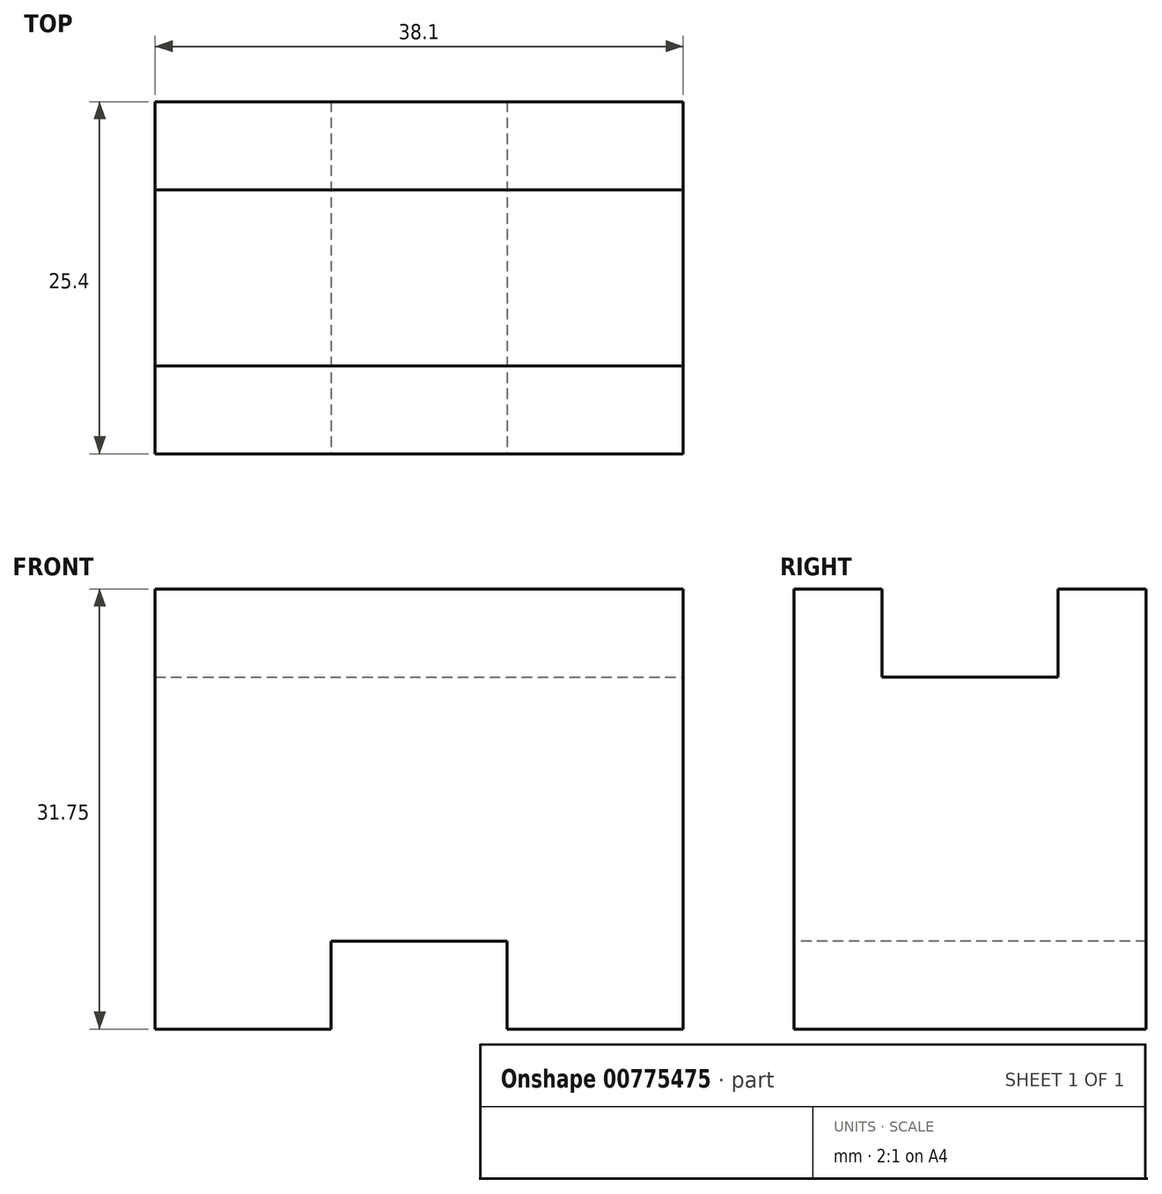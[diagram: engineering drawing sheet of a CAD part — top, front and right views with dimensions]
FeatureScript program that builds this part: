
annotation { "Feature Type Name" : "Feature", "Feature Type Description" : "" }
export const myFeature = defineFeature(function(context is Context, id is Id, definition is map)
    precondition{}
    {
        {
            var Q0;
            Q0=qCreatedBy(makeId("Front.planeOp"),FACE);
            var sketch = newSketch(context, id + "F0", { "sketchPlane" : qUnion([Q0])});
            skLineSegment(sketch, "E0", {"start": v(0, 0) * mm, "end": v(38.1, 0) * mm});
            skLineSegment(sketch, "E1", {"start": v(38.1, 0) * mm, "end": v(38.1, 31.75) * mm});
            skLineSegment(sketch, "E2", {"start": v(38.1, 31.75) * mm, "end": v(0, 31.75) * mm});
            skLineSegment(sketch, "E3", {"start": v(0, 31.75) * mm, "end": v(0, 0) * mm});
            skSolve(sketch);
        }
        {
            var Q0;
            Q0=makeQuery(id+"F0.imprint","IMPRINT",FACE,{"disambiguationData":[TD([[makeQuery(id+"F0.imprint","IMPRINT",EDGE,{"derivedFrom":sQuery(id+"F0.wireOp",EDGE,"E0")}),1.0]])]});
            extrude(context, id + "F1", {"entities" : qUnion([Q0]), "depth" : 25.4 * mm, "offsetDistance" : 25.4 * mm});
        }
        {
            var Q0;
            Q0=makeQuery(id+"F1.opExtrude","SWEPT_FACE",FACE,{"disambiguationData":[OSD([sQuery(id+"F0.wireOp",EDGE,"E1")])]});
            var sketch = newSketch(context, id + "F2", { "sketchPlane" : qUnion([Q0])});
            skLineSegment(sketch, "E4", {"start": v(-25.4, 31.75) * mm, "end": v(-19.05, 31.75) * mm});
            skLineSegment(sketch, "E5", {"start": v(0, 31.75) * mm, "end": v(-6.35, 31.75) * mm});
            skLineSegment(sketch, "E6", {"start": v(-6.35, 31.75) * mm, "end": v(-6.35, 25.4) * mm});
            skLineSegment(sketch, "E7", {"start": v(-6.35, 25.4) * mm, "end": v(-19.05, 25.4) * mm});
            skLineSegment(sketch, "E8", {"start": v(-19.05, 25.4) * mm, "end": v(-19.05, 31.75) * mm});
            skSolve(sketch);
        }
        {
            var Q0;
            {var subQ0=sQuery(id+"F2.wireOp",EDGE,"E6");Q0=makeQuery(id+"F2.imprint","IMPRINT",FACE,{"disambiguationData":[TD([[makeQuery(id+"F2.imprint","IMPRINT",EDGE,{"derivedFrom":subQ0}),-1.0]])]});}
            extrude(context, id + "F3", {"entities" : qUnion([Q0]), "operationType" : NewBodyOperationType.REMOVE, "oppositeDirection" : true, "depth" : 38.1 * mm, "offsetDistance" : 25.4 * mm});
        }
        {
            var Q0;
            Q0=makeQuery(id+"F1.opExtrude","CAP_FACE",FACE,{"disambiguationData":[OSD([sQuery(id+"F0.wireOp",EDGE,"E0"),sQuery(id+"F0.wireOp",EDGE,"E1"),sQuery(id+"F0.wireOp",EDGE,"E2"),sQuery(id+"F0.wireOp",EDGE,"E3")])],"isStart":false});
            var sketch = newSketch(context, id + "F4", { "sketchPlane" : qUnion([Q0])});
            skLineSegment(sketch, "E9", {"start": v(0, 0) * mm, "end": v(12.7, 0) * mm});
            skLineSegment(sketch, "E10", {"start": v(12.7, 0) * mm, "end": v(12.7, 6.35) * mm});
            skLineSegment(sketch, "E11", {"start": v(12.7, 6.35) * mm, "end": v(25.4, 6.35) * mm});
            skLineSegment(sketch, "E12", {"start": v(25.4, 6.35) * mm, "end": v(25.4, 0) * mm});
            skLineSegment(sketch, "E13", {"start": v(25.4, 0) * mm, "end": v(38.1, 0) * mm});
            skSolve(sketch);
        }
        {
            var Q0;
            {var subQ0=sQuery(id+"F4.wireOp",EDGE,"E10");Q0=makeQuery(id+"F4.imprint","IMPRINT",FACE,{"disambiguationData":[TD([[makeQuery(id+"F4.imprint","IMPRINT",EDGE,{"derivedFrom":subQ0}),-1.0]])]});}
            extrude(context, id + "F5", {"entities" : qUnion([Q0]), "operationType" : NewBodyOperationType.REMOVE, "oppositeDirection" : true, "depth" : 25.4 * mm, "offsetDistance" : 25.4 * mm});
        }
    });
